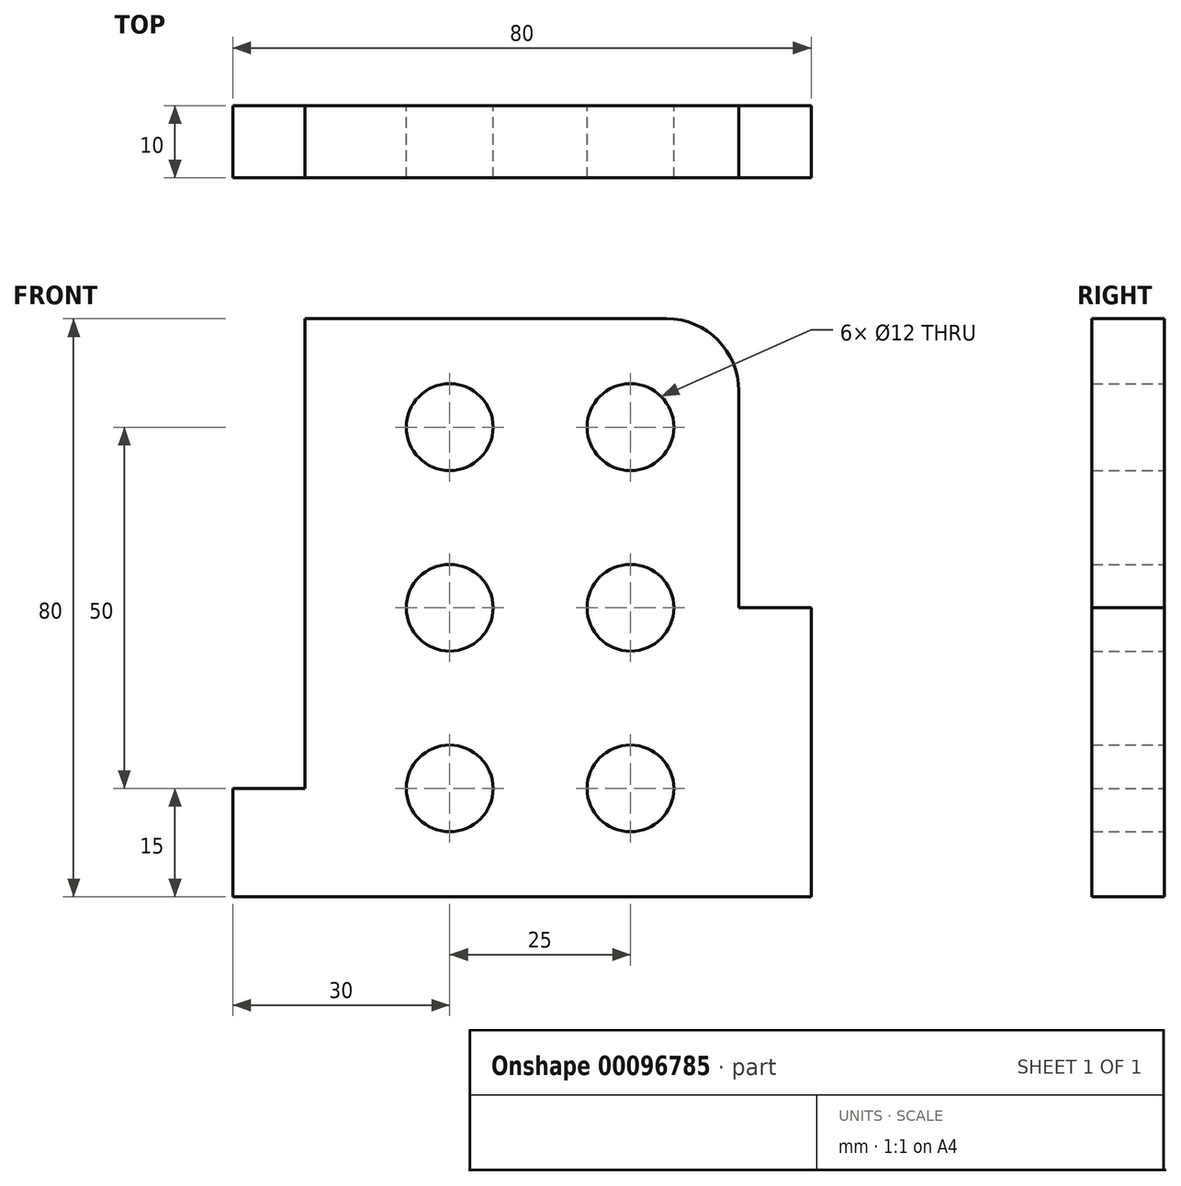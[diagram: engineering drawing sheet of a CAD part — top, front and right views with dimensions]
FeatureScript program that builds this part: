
annotation { "Feature Type Name" : "Feature", "Feature Type Description" : "" }
export const myFeature = defineFeature(function(context is Context, id is Id, definition is map)
    precondition{}
    {
        {
            var Q0;
            Q0=qCreatedBy(makeId("Front.planeOp"),FACE);
            var sketch = newSketch(context, id + "F0", { "sketchPlane" : qUnion([Q0])});
            skLineSegment(sketch, "E0", {"start": v(0, 0) * mm, "end": v(80, 0) * mm});
            skLineSegment(sketch, "E1", {"start": v(80, 0) * mm, "end": v(80, 40) * mm});
            skLineSegment(sketch, "E2", {"start": v(80, 40) * mm, "end": v(70, 40) * mm});
            skLineSegment(sketch, "E3", {"start": v(70, 40) * mm, "end": v(70, 70) * mm});
            skLineSegment(sketch, "E4", {"start": v(60, 80) * mm, "end": v(10, 80) * mm});
            skLineSegment(sketch, "E5", {"start": v(10, 80) * mm, "end": v(10, 15) * mm});
            skLineSegment(sketch, "E6", {"start": v(10, 15) * mm, "end": v(0, 15) * mm});
            skLineSegment(sketch, "E7", {"start": v(0, 15) * mm, "end": v(0, 0) * mm});
            skLineSegment(sketch, "E8", {"start": v(55, 80) * mm, "end": v(55, 0) * mm, "construction": true});
            skLineSegment(sketch, "E9", {"start": v(10, 15) * mm, "end": v(80, 15) * mm, "construction": true});
            skLineSegment(sketch, "E10", {"start": v(10, 65) * mm, "end": v(70, 65) * mm, "construction": true});
            skPoint(sketch, "E10.startSnap0", {"position": v(30, 65) * mm});
            skLineSegment(sketch, "E11", {"start": v(10, 40) * mm, "end": v(70, 40) * mm, "construction": true});
            skLineSegment(sketch, "E12", {"start": v(30, 80) * mm, "end": v(30, 0) * mm, "construction": true});
            skPoint(sketch, "E13.visualSharp", {"position": v(70, 80) * mm});
            skArc(sketch, "E13.filletArc", {"start": v(70, 70) * mm, "mid": v(67.07, 77.07) * mm, "end": v(60, 80) * mm});
            skCircle(sketch, "E14", {"center": v(30, 65) * mm, "radius": 6 * mm});
            skCircle(sketch, "E15", {"center": v(55, 65) * mm, "radius": 6 * mm});
            skCircle(sketch, "E16", {"center": v(30, 40) * mm, "radius": 6 * mm});
            skCircle(sketch, "E17", {"center": v(55, 40) * mm, "radius": 6 * mm});
            skCircle(sketch, "E18", {"center": v(30, 15) * mm, "radius": 6 * mm});
            skCircle(sketch, "E19", {"center": v(55, 15) * mm, "radius": 6 * mm});
            skSolve(sketch);
        }
        {
            var Q0;
            Q0 = qSketchRegion(id + "F0", true);
            extrude(context, id + "F1", {"entities" : qUnion([Q0]), "depth" : 10 * mm});
        }
    });
